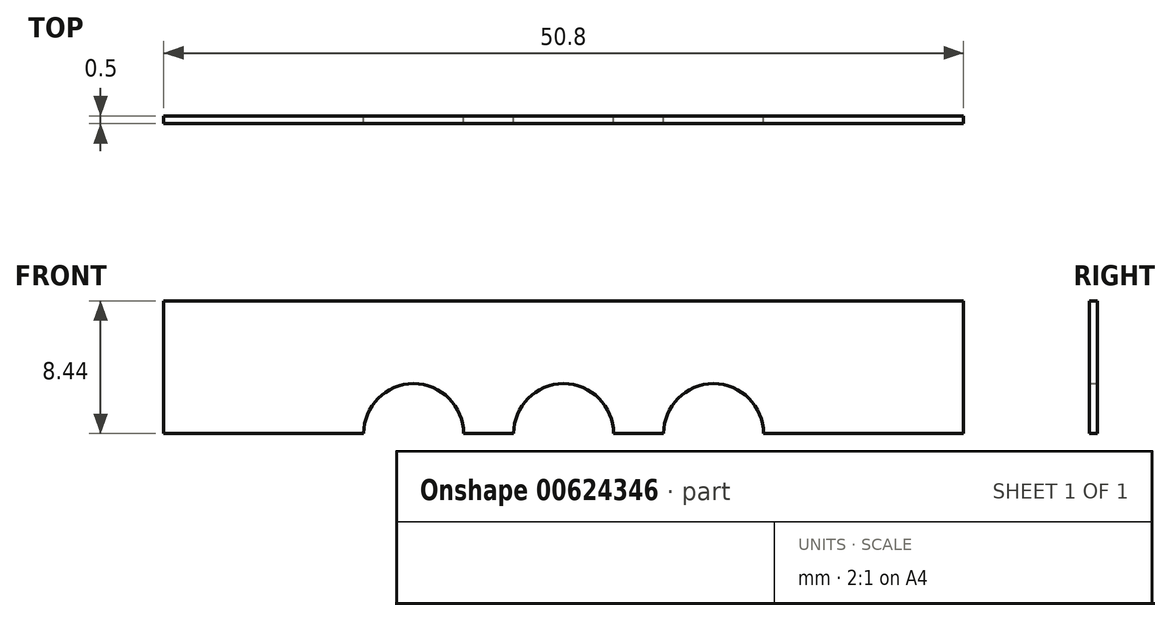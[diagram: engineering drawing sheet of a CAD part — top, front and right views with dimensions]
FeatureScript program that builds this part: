
annotation { "Feature Type Name" : "Feature", "Feature Type Description" : "" }
export const myFeature = defineFeature(function(context is Context, id is Id, definition is map)
    precondition{}
    {
        {
            assignVariable(context, id + "F0", {"name" : "HoleDiam", "anyValue" : .25});
        }
        {
            var Q0;
            Q0=qCreatedBy(makeId("Front.planeOp"),FACE);
            var sketch = newSketch(context, id + "F1", { "sketchPlane" : qUnion([Q0])});
            skLineSegment(sketch, "E0", {"start": v(-25.4, 0) * mm, "end": v(-25.4, 8.44) * mm});
            skLineSegment(sketch, "E1", {"start": v(-25.4, 8.44) * mm, "end": v(25.4, 8.44) * mm});
            skLineSegment(sketch, "E2", {"start": v(25.4, 8.44) * mm, "end": v(25.4, 0) * mm});
            skLineSegment(sketch, "E3", {"start": v(25.4, 0) * mm, "end": v(12.7, 0) * mm});
            skLineSegment(sketch, "E4", {"start": v(6.35, 0) * mm, "end": v(3.18, 0) * mm});
            skLineSegment(sketch, "E5", {"start": v(-3.18, 0) * mm, "end": v(-6.35, 0) * mm});
            skLineSegment(sketch, "E6", {"start": v(-25.4, 0) * mm, "end": v(-12.7, 0) * mm});
            skArc(sketch, "E7", {"start": v(-6.35, 0) * mm, "mid": v(-9.53, 3.17) * mm, "end": v(-12.7, 0) * mm});
            skArc(sketch, "E8", {"start": v(3.18, 0) * mm, "mid": v(0, 3.18) * mm, "end": v(-3.18, 0) * mm});
            skArc(sketch, "E9", {"start": v(12.7, 0) * mm, "mid": v(9.53, 3.18) * mm, "end": v(6.35, 0) * mm});
            skSolve(sketch);
        }
        {
            var Q0;
            Q0=makeQuery(id+"F1.imprint","IMPRINT",FACE,{"disambiguationData":[TD([[makeQuery(id+"F1.imprint","IMPRINT",EDGE,{"derivedFrom":sQuery(id+"F1.wireOp",EDGE,"E0")}),-1.0]])]});
            extrude(context, id + "F2", {"entities" : qUnion([Q0]), "depth" : (2 * getVariable(context, 'HoleDiam')) * mm, "offsetDistance" : 25.4 * mm});
        }
        {
            var Q0;
            Q0=makeQuery(id+"F2.opExtrude","SWEPT_FACE",FACE,{"disambiguationData":[OSD([sQuery(id+"F1.wireOp",EDGE,"E1")])]});
            var sketch = newSketch(context, id + "F3", { "sketchPlane" : qUnion([Q0])});
            skLineSegment(sketch, "E10.0", {"start": v(-25.4, -12.7) * mm, "end": v(-25.4, 0) * mm, "construction": true});
            skLineSegment(sketch, "E11.0", {"start": v(25.4, -12.7) * mm, "end": v(25.4, 0) * mm, "construction": true});
            skPoint(sketch, "E12", {"position": v(-19.05, -6.35) * mm});
            skPoint(sketch, "E13", {"position": v(19.05, -6.35) * mm});
            skLineSegment(sketch, "E14", {"start": v(-25.4, -6.35) * mm, "end": v(-19.05, -6.35) * mm, "construction": true});
            skLineSegment(sketch, "E15", {"start": v(19.05, -6.35) * mm, "end": v(25.4, -6.35) * mm, "construction": true});
            skSolve(sketch);
        }
        {
            var Q0;
            Q0=sQuery(id+"F3.wireOp",VERTEX,"E12");
            var Q1;
            Q1=sQuery(id+"F3.wireOp",VERTEX,"E13");
            var Q2;
            Q2=makeQuery(id+"F2.opExtrude","SWEPT_BODY",BODY,{"disambiguationData":[OSD([sQuery(id+"F1.wireOp",EDGE,"E0"),sQuery(id+"F1.wireOp",EDGE,"E1"),sQuery(id+"F1.wireOp",EDGE,"E2"),sQuery(id+"F1.wireOp",EDGE,"E3"),sQuery(id+"F1.wireOp",EDGE,"E4"),sQuery(id+"F1.wireOp",EDGE,"E5"),sQuery(id+"F1.wireOp",EDGE,"E6"),sQuery(id+"F1.wireOp",EDGE,"E7"),sQuery(id+"F1.wireOp",EDGE,"E8"),sQuery(id+"F1.wireOp",EDGE,"E9")])]});
            hole(context, id + "F4", {"style" : HoleStyle.SIMPLE, "endStyle" : HoleEndStyle.THROUGH, "holeDiameter" : (getVariable(context, 'HoleDiam')) * mm, "majorDiameter" : 6.35 * mm, "isTappedThrough" : true, "tappedDepth" : 12.7 * mm, "tapClearance" : 3, "locations" : qUnion([Q0, Q1]), "scope" : qUnion([Q2])});
        }
    });
